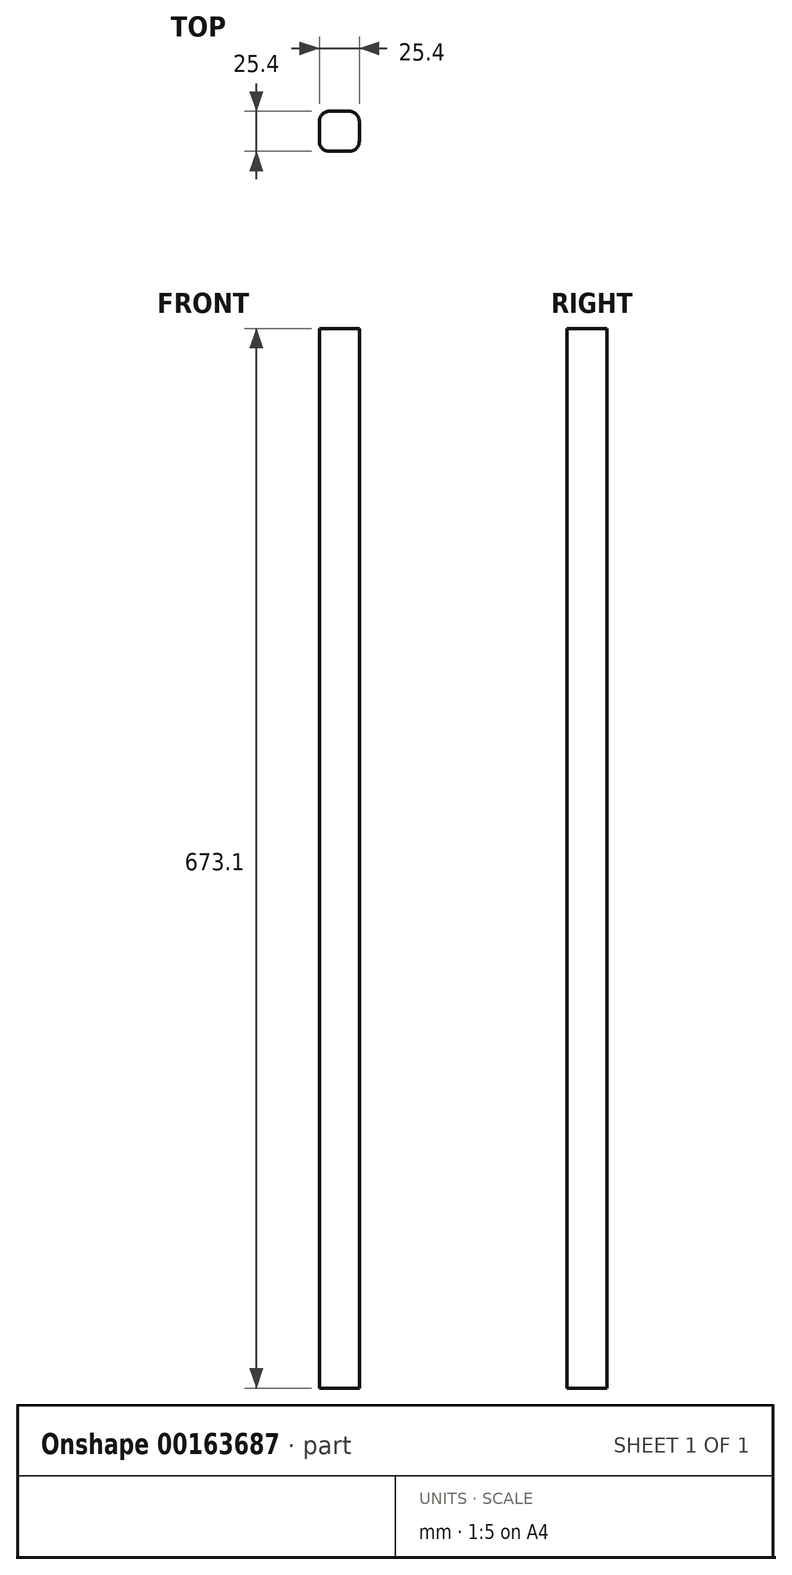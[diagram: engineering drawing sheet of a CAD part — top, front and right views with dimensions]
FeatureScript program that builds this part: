
annotation { "Feature Type Name" : "Feature", "Feature Type Description" : "" }
export const myFeature = defineFeature(function(context is Context, id is Id, definition is map)
    precondition{}
    {
        {
            var Q0;
            Q0=qCreatedBy(makeId("Top.planeOp"),FACE);
            var sketch = newSketch(context, id + "F0", { "sketchPlane" : qUnion([Q0])});
            skLineSegment(sketch, "E0.bottom", {"start": v(6.35, 12.7) * mm, "end": v(-6.35, 12.7) * mm});
            skLineSegment(sketch, "E0.top", {"start": v(6.35, -12.7) * mm, "end": v(-6.35, -12.7) * mm});
            skLineSegment(sketch, "E0.left", {"start": v(12.7, 6.35) * mm, "end": v(12.7, -6.35) * mm});
            skLineSegment(sketch, "E0.right", {"start": v(-12.7, 6.35) * mm, "end": v(-12.7, -6.35) * mm});
            skPoint(sketch, "E0.middle", {"position": v(0, 0) * mm});
            skPoint(sketch, "E1.visualSharp", {"position": v(-12.7, 12.7) * mm});
            skArc(sketch, "E1.filletArc", {"start": v(-6.35, 12.7) * mm, "mid": v(-10.84, 10.84) * mm, "end": v(-12.7, 6.35) * mm});
            skPoint(sketch, "E2.visualSharp", {"position": v(-12.7, -12.7) * mm});
            skArc(sketch, "E2.filletArc", {"start": v(-12.7, -6.35) * mm, "mid": v(-10.84, -10.84) * mm, "end": v(-6.35, -12.7) * mm});
            skPoint(sketch, "E3.visualSharp", {"position": v(12.7, -12.7) * mm});
            skArc(sketch, "E3.filletArc", {"start": v(6.35, -12.7) * mm, "mid": v(10.84, -10.84) * mm, "end": v(12.7, -6.35) * mm});
            skPoint(sketch, "E4.visualSharp", {"position": v(12.7, 12.7) * mm});
            skArc(sketch, "E4.filletArc", {"start": v(12.7, 6.35) * mm, "mid": v(10.84, 10.84) * mm, "end": v(6.35, 12.7) * mm});
            skSolve(sketch);
        }
        {
            var Q0;
            Q0=qSketchRegion(id+"F0",true);
            extrude(context, id + "F1", {"entities" : qUnion([Q0]), "depth" : 673.1 * mm, "offsetDistance" : 25.4 * mm});
        }
    });
